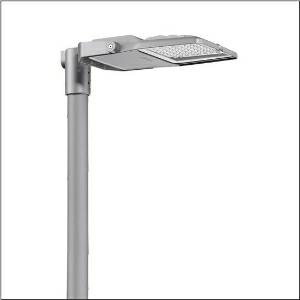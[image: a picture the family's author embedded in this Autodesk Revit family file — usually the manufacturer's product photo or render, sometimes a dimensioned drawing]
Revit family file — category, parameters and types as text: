
# Revit family: floodlight_fl_21_iq_mini___pl33t_5xa7772b2f3a_3cf2
name_source: partatom
category: Lighting Fixtures
units: mm (PartAtom-declared; Revit-internal decimal feet)

## family parameters
Cut with Voids When Loaded = No
Host = Face
Light Source = No
Part Type = Normal
Room Calculation Point = No
Round Connector Dimension = Use Diameter
Shared = No

## types (1)
- --- (1 x LED, 6170 lm, 45.5 W, 3000K)
    Apparent Load = 46 VA
    CIE Flux Codes = 26 75 99 100 100
    Color Rendering = 70
    Color Temperature = 3000K
    Default Elevation = 1800 mm
    Description = Floodlight FL 21 iQ mini, floodlight, primary light control with lens, of PMMA, primary optical cover: protective disc, of toughened safety glass, transparent, light distribution: PL33T, light emission: direct distribution, installation type: surface-mounted, LED, High Power LED, rated luminous flux: 6.170lm, luminous efficacy: 136lm/W, light colour: 730, colour temperature: 3000K, control gear: iQ Street-Remote/DALI, control: Auto-Match, Temp-Guard, Night-Set, Smart-Wire, Desk-Remote (wireless, voltage-free reading and setting of iQ features in the workshop via application-optimized NFC function/RFID function), optimised constant luminous flux control (CLO 2.0), Light-Fading, Lumen-Switch, with terminal, 6-pole, mains connection: 220..240V, AC, 50/60Hz, start of lifetime: 46W, end of service life: 48W, reduction: 22W, luminaire housing, of diecast aluminium, powder-coated, Siteco® metallic grey (DB 702S), corrosivity category C5 mid according to DIN EN ISO 12944, suitable for swimming pools, chlorine-resistant, sealing non-destructively replaceable, please order mast flange separately, mast bracket, of steel, galvanised, powder-coated, protection rating (complete): IP66, insulation class (complete): insulation class II (safety insulation), certification: CE, ENEC, VDE, protection symbol: D, impact resistance: IK08, permissible operating ambient temperature: -40..+40°C, permissible operating ambient temperature for outdoor applications: -40..+50°C, standard: DIN EN 12944, LABS conformity tested according to VDMA 24364:2018-05, packaging unit: 1 piece

Light Distribution: PL33T
    Height = 70 mm
    Lamp = 1 x LED
    Lamp Light Flux = 6170 lm
    Lamp Power = 45.5 W
    Lamp count = 1
    Length = 485 mm
    Luminous efficacy = 136 lm/W
    Manufacturer = Siteco
    ModVariant = No
    Model = 5XA7772B2F3A
    Number of Poles = 1
    OnlyDefault = Yes
    Power Factor = 1
    Product Name = Floodlight FL 21 iQ mini | PL33T
    Product group = floodlight | pylon annexe
    ProductGroupID = 6200
    Protection Class = Protection class II
    Protection Degree = IP 66
    RLX_Detail_Level = 1
    RLX_Emergency_Light_Flux = 0 lm
    RLX_Emergency_Type = 0
    RLX_Emergency_Type_DB = No
    RlxData = <blob elided: 101165 chars, md5=4567d2ac>
    Socket = socket
    Standby Power = 0 W
    System Light Flux = 6170 lm
    System Power = 46 W
    Type Comments = factory setting: luminous flux: 100 % | dim-lin: 254 | 463 mA
    Type Image = l_1007125.jpg
    URL = http://relux.com
    VarID = @adj_150032
    Voltage = 0 V
    Weight = 0.00 kg
    Width = 337 mm

## geometry (parser evidence)
native form markers: Blend x4, Sweep x12
no freeform markers — native parametric forms only
